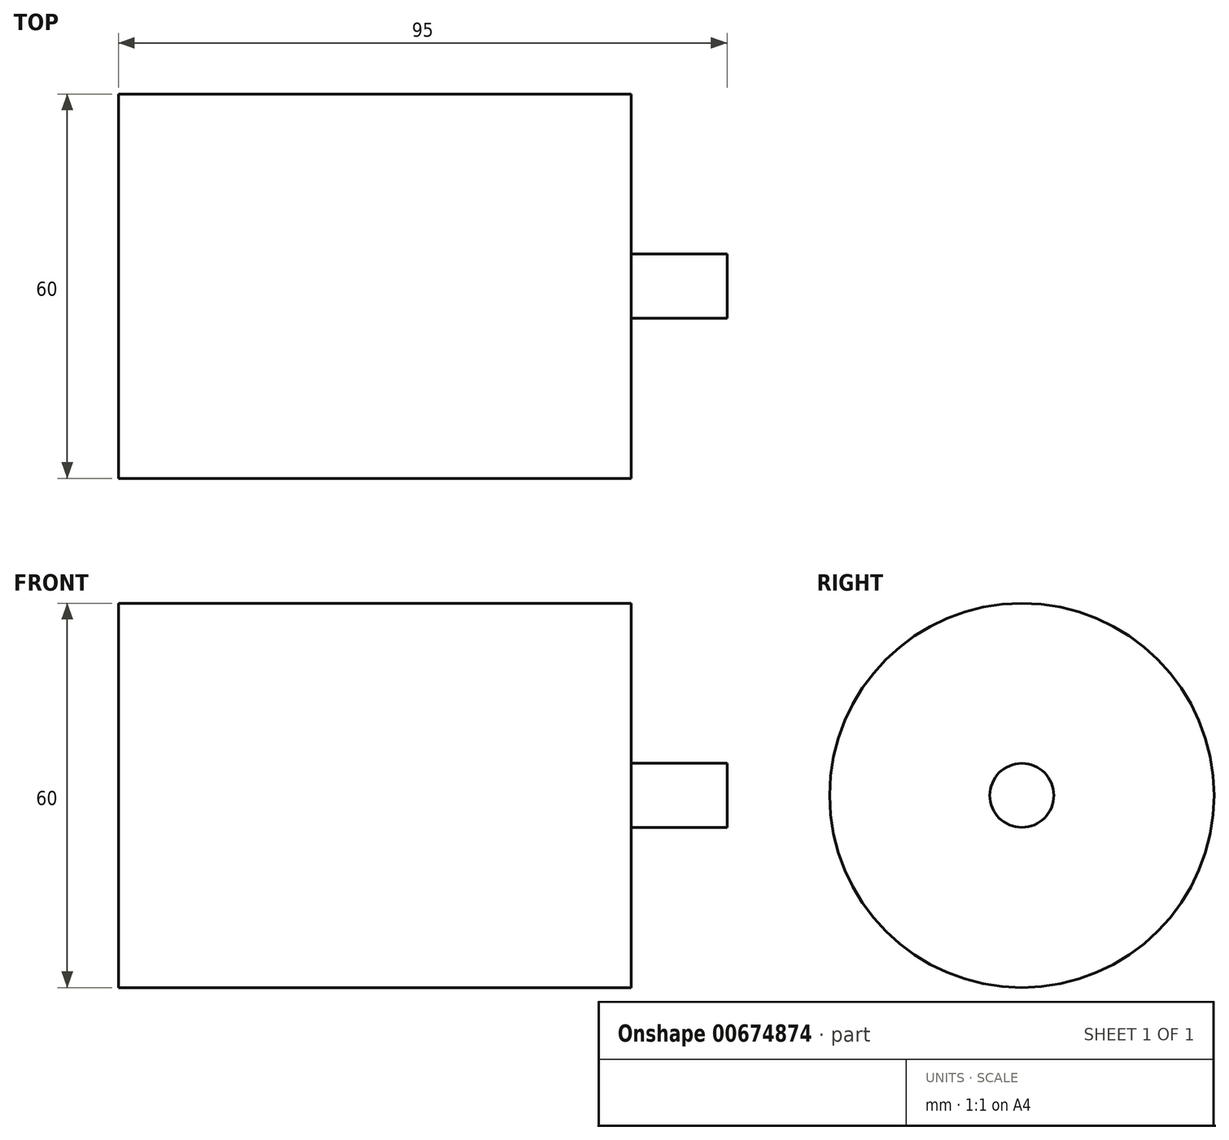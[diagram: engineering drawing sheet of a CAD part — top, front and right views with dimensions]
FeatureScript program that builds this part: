
annotation { "Feature Type Name" : "Feature", "Feature Type Description" : "" }
export const myFeature = defineFeature(function(context is Context, id is Id, definition is map)
    precondition{}
    {
        {
            var Q0;
            Q0=qCreatedBy(makeId("Front.planeOp"),FACE);
            var sketch = newSketch(context, id + "F0", { "sketchPlane" : qUnion([Q0])});
            skLineSegment(sketch, "E0", {"start": v(0, 0) * mm, "end": v(0, 30) * mm});
            skLineSegment(sketch, "E1", {"start": v(0, 30) * mm, "end": v(80, 30) * mm});
            skLineSegment(sketch, "E2", {"start": v(80, 30) * mm, "end": v(80, 5) * mm});
            skLineSegment(sketch, "E3", {"start": v(80, 5) * mm, "end": v(95, 5) * mm});
            skLineSegment(sketch, "E4", {"start": v(95, 5) * mm, "end": v(95, 0) * mm});
            skLineSegment(sketch, "E5", {"start": v(95, 0) * mm, "end": v(0, 0) * mm});
            skLineSegment(sketch, "E6", {"start": v(-41.27, 0) * mm, "end": v(56.33, 0) * mm, "construction": true});
            skSolve(sketch);
        }
        {
            var Q0;
            Q0=makeQuery(id+"F0.imprint","IMPRINT",FACE,{"disambiguationData":[TD([[makeQuery(id+"F0.imprint","IMPRINT",EDGE,{"derivedFrom":sQuery(id+"F0.wireOp",EDGE,"E0")}),-1.0]])]});
            var Q1;
            Q1=sQuery(id+"F0.wireOp",EDGE,"E6");
            revolve(context, id + "F1", {"entities" : qUnion([Q0]), "axis" : qUnion([Q1]), "revolveType" : RevolveType.FULL});
        }
    });
